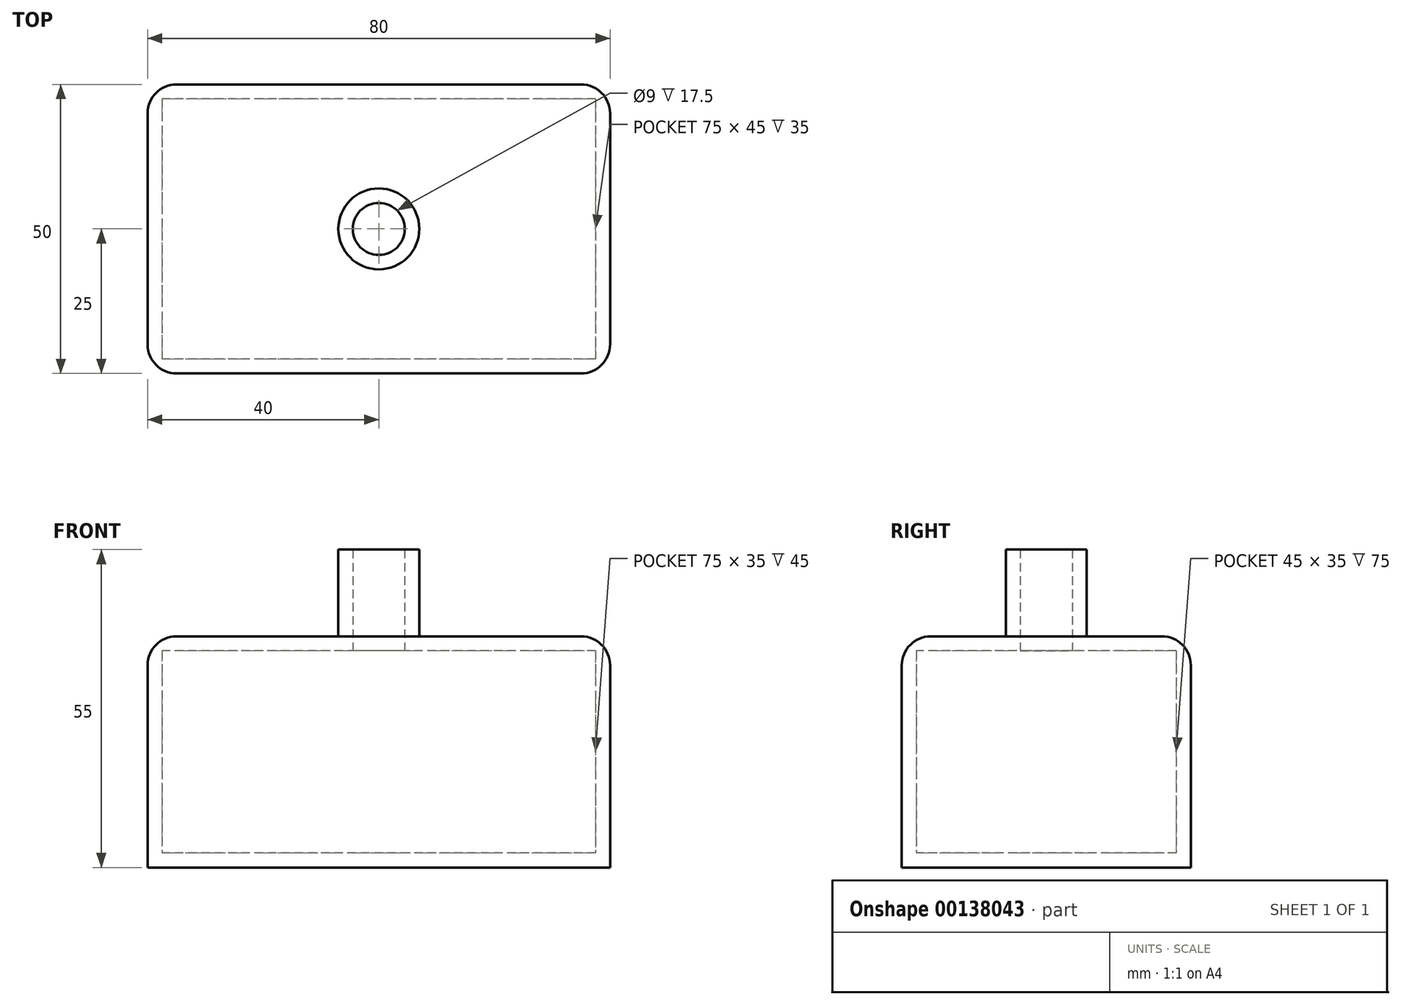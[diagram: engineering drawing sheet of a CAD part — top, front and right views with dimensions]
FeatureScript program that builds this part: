
annotation { "Feature Type Name" : "Feature", "Feature Type Description" : "" }
export const myFeature = defineFeature(function(context is Context, id is Id, definition is map)
    precondition{}
    {
        {
            var Q0;
            Q0=qCreatedBy(makeId("Top.planeOp"),FACE);
            var sketch = newSketch(context, id + "F0", { "sketchPlane" : qUnion([Q0])});
            skLineSegment(sketch, "E0.bottom", {"start": v(40, 25) * mm, "end": v(-40, 25) * mm});
            skLineSegment(sketch, "E0.top", {"start": v(40, -25) * mm, "end": v(-40, -25) * mm});
            skLineSegment(sketch, "E0.left", {"start": v(40, 25) * mm, "end": v(40, -25) * mm});
            skLineSegment(sketch, "E0.right", {"start": v(-40, 25) * mm, "end": v(-40, -25) * mm});
            skPoint(sketch, "E0.middle", {"position": v(0, 0) * mm});
            skSolve(sketch);
        }
        {
            var Q0;
            Q0=makeQuery(id+"F0.imprint","IMPRINT",FACE,{"disambiguationData":[TD([[makeQuery(id+"F0.imprint","IMPRINT",EDGE,{"derivedFrom":sQuery(id+"F0.wireOp",EDGE,"E0.bottom")}),1.0]])]});
            extrude(context, id + "F1", {"entities" : qUnion([Q0]), "depth" : 40 * mm});
        }
        {
            var Q0;
            Q0=makeQuery(id+"F1.opExtrude","CAP_FACE",FACE,{"disambiguationData":[OSD([sQuery(id+"F0.wireOp",EDGE,"E0.bottom"),sQuery(id+"F0.wireOp",EDGE,"E0.top"),sQuery(id+"F0.wireOp",EDGE,"E0.left"),sQuery(id+"F0.wireOp",EDGE,"E0.right")])],"isStart":false});
            var sketch = newSketch(context, id + "F2", { "sketchPlane" : qUnion([Q0])});
            skCircle(sketch, "E1", {"center": v(0, 0) * mm, "radius": 7 * mm});
            skSolve(sketch);
        }
        {
            var Q0;
            Q0=makeQuery(id+"F2.imprint","IMPRINT",FACE,{"disambiguationData":[TD([[makeQuery(id+"F2.imprint","IMPRINT",EDGE,{"derivedFrom":sQuery(id+"F2.wireOp",EDGE,"E1")}),1.0]])]});
            extrude(context, id + "F3", {"entities" : qUnion([Q0]), "operationType" : NewBodyOperationType.ADD, "depth" : 15 * mm});
        }
        {
            var Q0;
            Q0=makeQuery(id+"F3.opExtrude","CAP_FACE",FACE,{"disambiguationData":[OSD([sQuery(id+"F2.wireOp",EDGE,"E1")])],"isStart":false});
            shell(context, id + "F4", {"entities" : qUnion([Q0]), "thickness" : 2.5 * mm});
        }
        {
            var Q0;
            Q0=makeQuery(id+"F3.opExtrude","CAP_EDGE",EDGE,{"disambiguationData":[OSD([sQuery(id+"F2.wireOp",EDGE,"E1")])],"isStart":true});
            var Q1;
            Q1=makeQuery(id+"F1.opExtrude","CAP_EDGE",EDGE,{"disambiguationData":[OSD([sQuery(id+"F0.wireOp",EDGE,"E0.top")])],"isStart":false});
            var Q2;
            Q2=makeQuery(id+"F1.opExtrude","CAP_EDGE",EDGE,{"disambiguationData":[OSD([sQuery(id+"F0.wireOp",EDGE,"E0.left")])],"isStart":false});
            var Q3;
            Q3=makeQuery(id+"F1.opExtrude","CAP_EDGE",EDGE,{"disambiguationData":[OSD([sQuery(id+"F0.wireOp",EDGE,"E0.right")])],"isStart":false});
            var Q4;
            Q4=makeQuery(id+"F1.opExtrude","CAP_EDGE",EDGE,{"disambiguationData":[OSD([sQuery(id+"F0.wireOp",EDGE,"E0.bottom")])],"isStart":false});
            var Q5;
            Q5=makeQuery(id+"F1.opExtrude","SWEPT_EDGE",EDGE,{"disambiguationData":[OSD([sQuery(id+"F0.wireOp",EDGE,"E0.top"),sQuery(id+"F0.wireOp",EDGE,"E0.right")])]});
            var Q6;
            Q6=makeQuery(id+"F1.opExtrude","SWEPT_EDGE",EDGE,{"disambiguationData":[OSD([sQuery(id+"F0.wireOp",EDGE,"E0.top"),sQuery(id+"F0.wireOp",EDGE,"E0.left")])]});
            var Q7;
            Q7=makeQuery(id+"F1.opExtrude","SWEPT_EDGE",EDGE,{"disambiguationData":[OSD([sQuery(id+"F0.wireOp",EDGE,"E0.bottom"),sQuery(id+"F0.wireOp",EDGE,"E0.right")])]});
            var Q8;
            Q8=makeQuery(id+"F1.opExtrude","SWEPT_EDGE",EDGE,{"disambiguationData":[OSD([sQuery(id+"F0.wireOp",EDGE,"E0.bottom"),sQuery(id+"F0.wireOp",EDGE,"E0.left")])]});
            fillet(context, id + "F5", {"entities" : qUnion([Q0, Q1, Q2, Q3, Q4, Q5, Q6, Q7, Q8]), "radius" : 5 * mm, "tangentPropagation" : true, "allowEdgeOverflow" : false});
        }
    });
